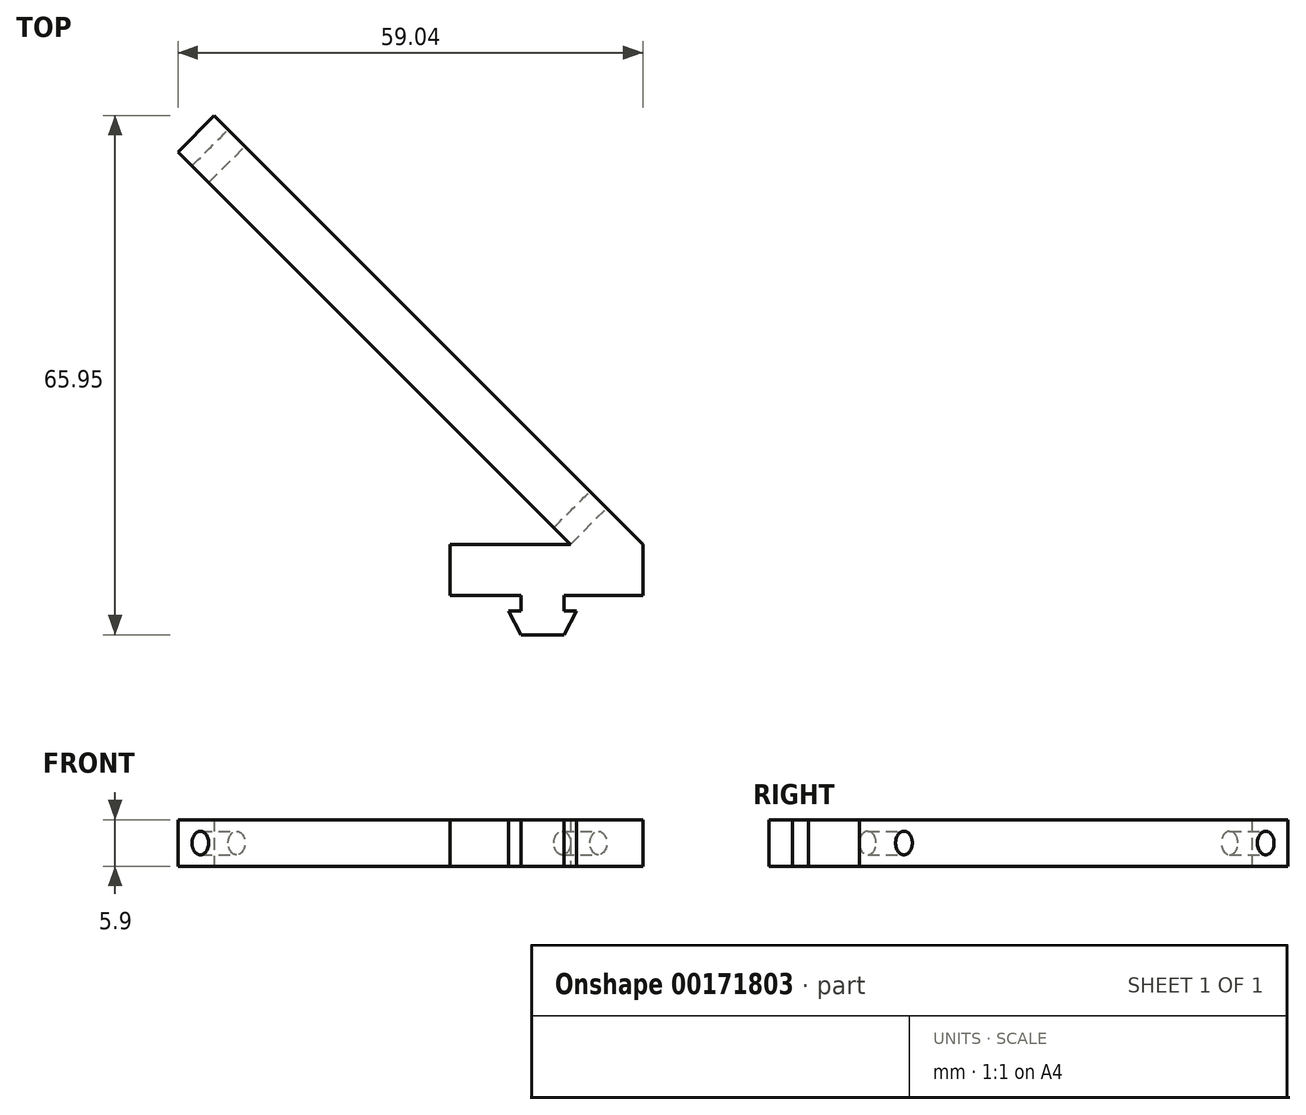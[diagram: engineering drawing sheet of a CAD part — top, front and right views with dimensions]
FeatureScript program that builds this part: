
annotation { "Feature Type Name" : "Feature", "Feature Type Description" : "" }
export const myFeature = defineFeature(function(context is Context, id is Id, definition is map)
    precondition{}
    {
        {
            var Q0;
            Q0=qCreatedBy(makeId("Top.planeOp"),FACE);
            var sketch = newSketch(context, id + "F0", { "sketchPlane" : qUnion([Q0])});
            skLineSegment(sketch, "E0.bottom", {"start": v(0, 0) * mm, "end": v(-10, 0) * mm});
            skLineSegment(sketch, "E0.top", {"start": v(-9.2, 6.5) * mm, "end": v(-24.5, 6.5) * mm});
            skLineSegment(sketch, "E0.left", {"start": v(0, 0) * mm, "end": v(0, 6.5) * mm});
            skLineSegment(sketch, "E0.right", {"start": v(-24.5, 0) * mm, "end": v(-24.5, 6.5) * mm});
            skLineSegment(sketch, "E1", {"start": v(0, 6.5) * mm, "end": v(-54.45, 60.95) * mm});
            skLineSegment(sketch, "E2", {"start": v(-54.45, 60.95) * mm, "end": v(-59.04, 56.35) * mm});
            skLineSegment(sketch, "E3", {"start": v(-59.04, 56.35) * mm, "end": v(-9.2, 6.5) * mm});
            skLineSegment(sketch, "E4", {"start": v(-15.5, 0) * mm, "end": v(-15.5, -2) * mm});
            skLineSegment(sketch, "E5", {"start": v(-15.5, -2) * mm, "end": v(-17.05, -2) * mm});
            skLineSegment(sketch, "E6", {"start": v(-17.05, -2) * mm, "end": v(-15.5, -5) * mm});
            skLineSegment(sketch, "E7", {"start": v(-15.5, -5) * mm, "end": v(-10, -5) * mm});
            skLineSegment(sketch, "E8", {"start": v(-10, -5) * mm, "end": v(-8.45, -2) * mm});
            skLineSegment(sketch, "E9", {"start": v(-8.45, -2) * mm, "end": v(-10, -2) * mm});
            skLineSegment(sketch, "E10", {"start": v(-10, -2) * mm, "end": v(-10, 0) * mm});
            skLineSegment(sketch, "E11.trimOffspring", {"start": v(-15.5, 0) * mm, "end": v(-24.5, 0) * mm});
            skLineSegment(sketch, "E12", {"start": v(-12.5, 5.32) * mm, "end": v(-2.58, 15.24) * mm, "construction": true});
            skSolve(sketch);
        }
        {
            var Q0;
            Q0=makeQuery(id+"F0.imprint","IMPRINT",FACE,{"disambiguationData":[TD([[makeQuery(id+"F0.imprint","IMPRINT",EDGE,{"derivedFrom":sQuery(id+"F0.wireOp",EDGE,"E0.bottom")}),-1.0]])]});
            extrude(context, id + "F1", {"entities" : qUnion([Q0]), "depth" : 5.9 * mm});
        }
        {
            var Q0;
            Q0=makeQuery(id+"F1.opExtrude","SWEPT_FACE",FACE,{"disambiguationData":[OSD([sQuery(id+"F0.wireOp",EDGE,"E1")])]});
            var sketch = newSketch(context, id + "F2", { "sketchPlane" : qUnion([Q0])});
            skCircle(sketch, "E13", {"center": v(12.6, 2.95) * mm, "radius": 1.5 * mm});
            skPoint(sketch, "E13.centerSnap0", {"position": v(4.6, 2.95) * mm});
            skCircle(sketch, "E14", {"center": v(77.6, 2.95) * mm, "radius": 1.5 * mm});
            skSolve(sketch);
        }
        {
            var Q0;
            Q0=makeQuery(id+"F2.imprint","IMPRINT",FACE,{"disambiguationData":[TD([[makeQuery(id+"F2.imprint","IMPRINT",EDGE,{"derivedFrom":sQuery(id+"F2.wireOp",EDGE,"E14")}),1.0]])]});
            var Q1;
            Q1=makeQuery(id+"F2.imprint","IMPRINT",FACE,{"disambiguationData":[TD([[makeQuery(id+"F2.imprint","IMPRINT",EDGE,{"derivedFrom":sQuery(id+"F2.wireOp",EDGE,"E13")}),1.0]])]});
            extrude(context, id + "F3", {"entities" : qUnion([Q0, Q1]), "operationType" : NewBodyOperationType.REMOVE, "endBound" : BoundingType.UP_TO_NEXT, "oppositeDirection" : true, "depth" : 25 * mm});
        }
    });
